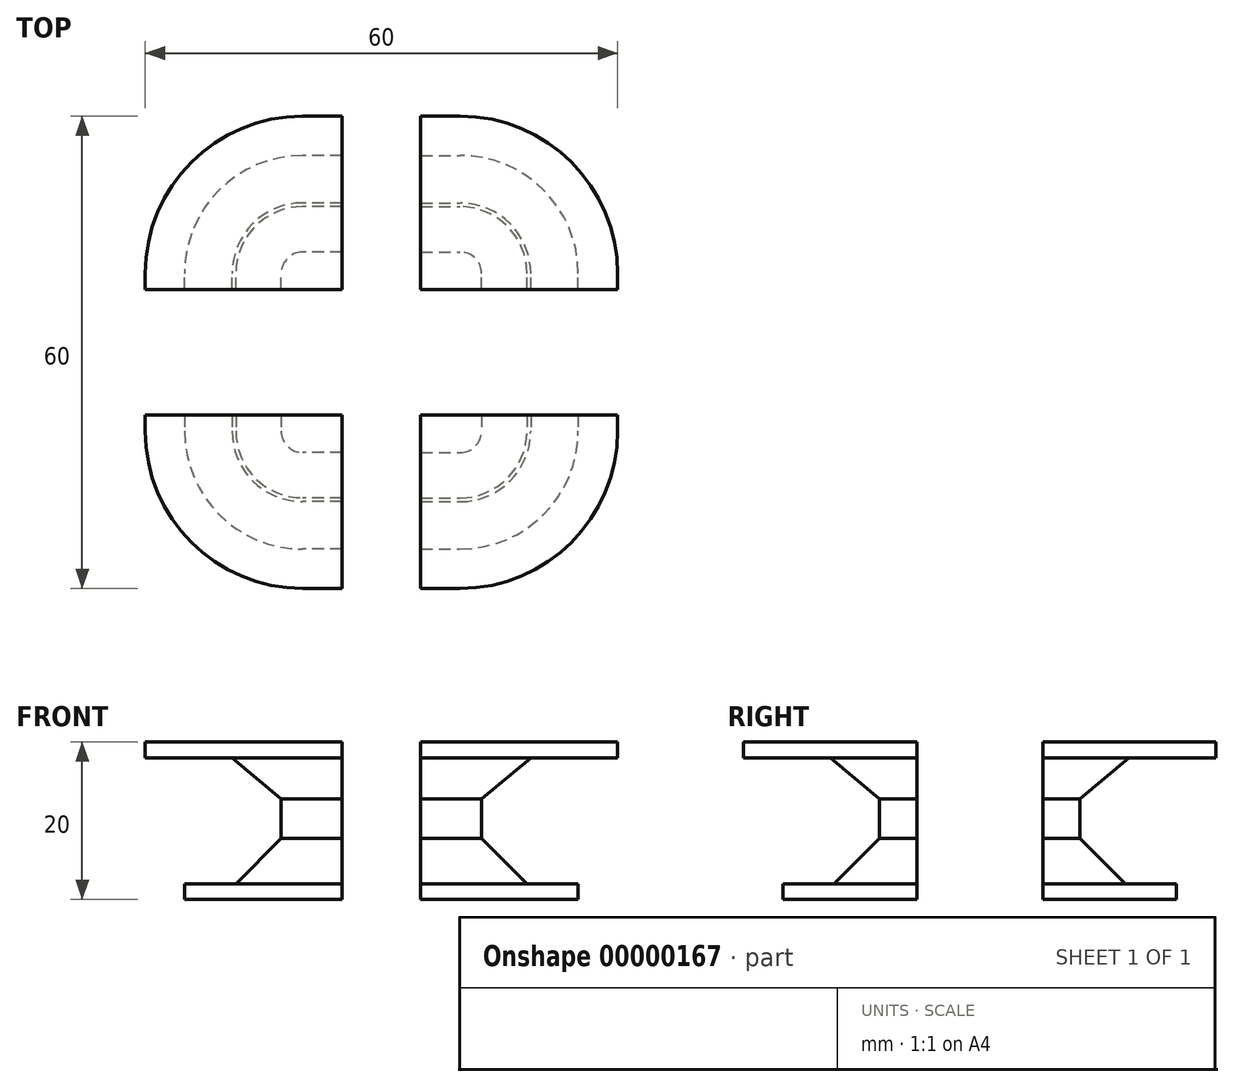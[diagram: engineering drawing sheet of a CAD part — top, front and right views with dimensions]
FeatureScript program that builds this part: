
annotation { "Feature Type Name" : "Feature", "Feature Type Description" : "" }
export const myFeature = defineFeature(function(context is Context, id is Id, definition is map)
    precondition{}
    {
        {
            var Q0;
            Q0      = qCreatedBy(makeId("Right.planeOp"), FACE);
            var sketch = newSketch(context, id + "F0", { "sketchPlane" : qUnion([Q0])});
            skLineSegment(sketch, "E0", {"start": v(0, 0) * mm, "end": v(0, 20) * mm});
            skLineSegment(sketch, "E1", {"start": v(0, 20) * mm, "end": v(-20, 20) * mm});
            skLineSegment(sketch, "E2", {"start": v(-20, 20) * mm, "end": v(-20, 18) * mm});
            skLineSegment(sketch, "E3", {"start": v(-20, 18) * mm, "end": v(-8.97, 18) * mm});
            skLineSegment(sketch, "E4", {"start": v(-8.97, 18) * mm, "end": v(-2.73, 12.76) * mm});
            skLineSegment(sketch, "E5", {"start": v(-2.73, 12.76) * mm, "end": v(-2.73, 7.76) * mm});
            skLineSegment(sketch, "E6", {"start": v(-2.73, 7.76) * mm, "end": v(-8.5, 2) * mm});
            skLineSegment(sketch, "E7", {"start": v(-8.5, 2) * mm, "end": v(-15, 2) * mm});
            skLineSegment(sketch, "E8", {"start": v(-15, 2) * mm, "end": v(-15, 0) * mm});
            skLineSegment(sketch, "E9", {"start": v(-15, 0) * mm, "end": v(0, 0) * mm});
            skLineSegment(sketch, "E10", {"start": v(-2.73, 12.76) * mm, "end": v(0, 12.76) * mm, "construction": true});
            skLineSegment(sketch, "E11", {"start": v(-2.73, 7.76) * mm, "end": v(0, 7.76) * mm, "construction": true});
            skSolve(sketch);
        }
        {
            var Q0;
            Q0=makeQuery(id+"F0.imprint","IMPRINT",FACE,{"disambiguationData":[TD([[makeQuery(id+"F0.imprint","IMPRINT",EDGE,{"derivedFrom":sQuery(id+"F0.wireOp",EDGE,"E0")}),1.0]])]});
            extrude(context, id + "F1", {"entities" : qUnion([Q0]), "depth" : 5 * mm});
        }
        {
            var Q0;
            Q0=makeQuery(id+"F0.imprint","IMPRINT",FACE,{"disambiguationData":[TD([[makeQuery(id+"F0.imprint","IMPRINT",EDGE,{"derivedFrom":sQuery(id+"F0.wireOp",EDGE,"E0")}),1.0]])]});
            var Q1;
            Q1=makeQuery(id+"F1.opExtrude","CAP_EDGE",EDGE,{"disambiguationData":[OSD([sQuery(id+"F0.wireOp",EDGE,"E0")])],"isStart":true});
            revolve(context, id + "F2", {"operationType" : NewBodyOperationType.ADD, "entities" : qUnion([Q0]), "axis" : qUnion([Q1]), "revolveType" : RevolveType.ONE_DIRECTION, "oppositeDirection" : true, "angle" : 90 * degree});
        }
        {
            var Q0;
            {var subQ0=sQuery(id+"F0.wireOp",EDGE,"E0");Q0=makeQuery(id+"F2.boolean.opBoolean","MERGE",FACE,{"derivedFrom":[makeQuery(id+"F1.opExtrude","SWEPT_FACE",FACE,{"disambiguationData":[OSD([subQ0])]}),makeQuery(id+"F2.opRevolve","CAP_FACE",FACE,{"disambiguationData":[OSD([subQ0,sQuery(id+"F0.wireOp",EDGE,"E1"),sQuery(id+"F0.wireOp",EDGE,"E2"),sQuery(id+"F0.wireOp",EDGE,"E3"),sQuery(id+"F0.wireOp",EDGE,"E4"),sQuery(id+"F0.wireOp",EDGE,"E5"),sQuery(id+"F0.wireOp",EDGE,"E6"),sQuery(id+"F0.wireOp",EDGE,"E7"),sQuery(id+"F0.wireOp",EDGE,"E8"),sQuery(id+"F0.wireOp",EDGE,"E9")])],"isStart":false})]});}
            extrude(context, id + "F3", {"entities" : qUnion([Q0]), "operationType" : NewBodyOperationType.ADD, "depth" : 2 * mm});
        }
        {
            var Q0;
            Q0=qCreatedBy(makeId("Right.planeOp"),FACE);
            cPlane(context, id + "F4", {"entities" : qUnion([Q0]), "cplaneType" : CPlaneType.OFFSET, "offset" : 10 * mm, "width" : 150 * mm, "height" : 150 * mm});
        }
        {
            var Q0;
            Q0=makeQuery(id+"F1.opExtrude","SWEPT_BODY",BODY,{"disambiguationData":[OSD([sQuery(id+"F0.wireOp",EDGE,"E0"),sQuery(id+"F0.wireOp",EDGE,"E1"),sQuery(id+"F0.wireOp",EDGE,"E2"),sQuery(id+"F0.wireOp",EDGE,"E3"),sQuery(id+"F0.wireOp",EDGE,"E4"),sQuery(id+"F0.wireOp",EDGE,"E5"),sQuery(id+"F0.wireOp",EDGE,"E6"),sQuery(id+"F0.wireOp",EDGE,"E7"),sQuery(id+"F0.wireOp",EDGE,"E8"),sQuery(id+"F0.wireOp",EDGE,"E9")])]});
            var Q1;
            Q1=qCreatedBy(id+"F4.planeOp",FACE);
            mirror(context, id + "F5", {"entities" : qUnion([Q0]), "mirrorPlane" : qUnion([Q1])});
        }
        {
            var Q0;
            Q0=qCreatedBy(makeId("Front.planeOp"),FACE);
            cPlane(context, id + "F6", {"entities" : qUnion([Q0]), "cplaneType" : CPlaneType.OFFSET, "offset" : 10 * mm, "oppositeDirection" : true, "width" : 150 * mm, "height" : 150 * mm});
        }
        {
            var Q0;
            Q0=makeQuery(id+"F1.opExtrude","SWEPT_BODY",BODY,{"disambiguationData":[OSD([sQuery(id+"F0.wireOp",EDGE,"E0"),sQuery(id+"F0.wireOp",EDGE,"E1"),sQuery(id+"F0.wireOp",EDGE,"E2"),sQuery(id+"F0.wireOp",EDGE,"E3"),sQuery(id+"F0.wireOp",EDGE,"E4"),sQuery(id+"F0.wireOp",EDGE,"E5"),sQuery(id+"F0.wireOp",EDGE,"E6"),sQuery(id+"F0.wireOp",EDGE,"E7"),sQuery(id+"F0.wireOp",EDGE,"E8"),sQuery(id+"F0.wireOp",EDGE,"E9")])]});
            var Q1;
            Q1=makeQuery(id+"F5.opPattern","COPY",BODY,{"derivedFrom":makeQuery(id+"F1.opExtrude","SWEPT_BODY",BODY,{"disambiguationData":[OSD([sQuery(id+"F0.wireOp",EDGE,"E0"),sQuery(id+"F0.wireOp",EDGE,"E1"),sQuery(id+"F0.wireOp",EDGE,"E2"),sQuery(id+"F0.wireOp",EDGE,"E3"),sQuery(id+"F0.wireOp",EDGE,"E4"),sQuery(id+"F0.wireOp",EDGE,"E5"),sQuery(id+"F0.wireOp",EDGE,"E6"),sQuery(id+"F0.wireOp",EDGE,"E7"),sQuery(id+"F0.wireOp",EDGE,"E8"),sQuery(id+"F0.wireOp",EDGE,"E9")])]}),"instanceName":"1"});
            var Q2;
            Q2=qCreatedBy(id+"F6.planeOp",FACE);
            mirror(context, id + "F7", {"entities" : qUnion([Q0, Q1]), "mirrorPlane" : qUnion([Q2])});
        }
    });
